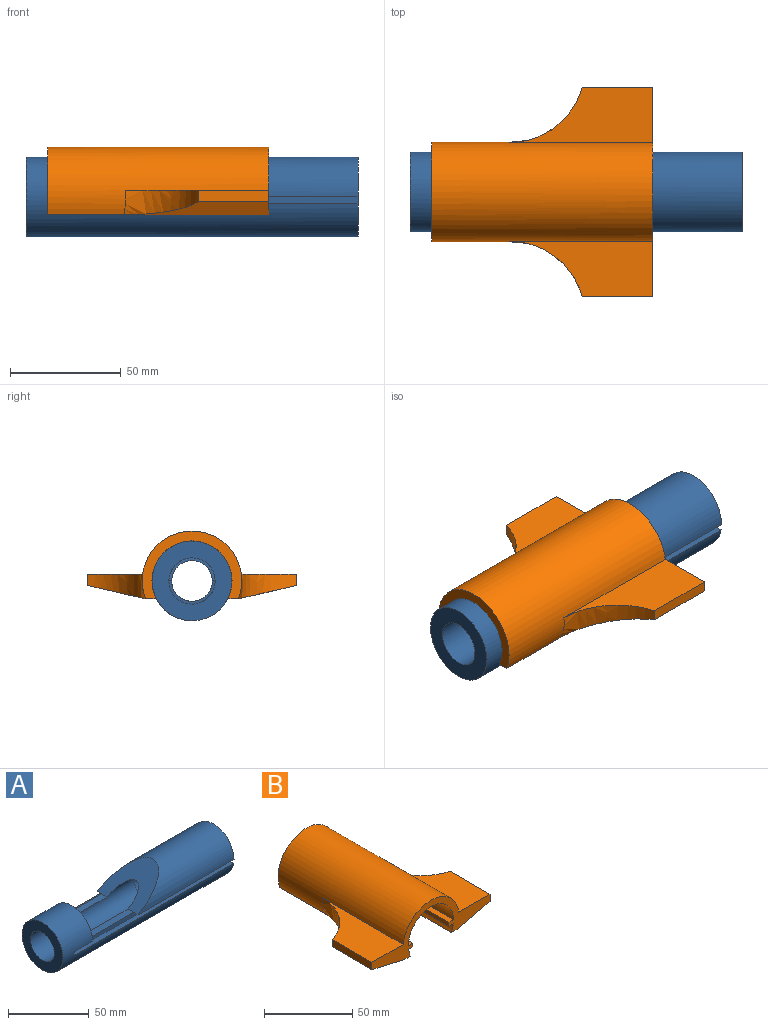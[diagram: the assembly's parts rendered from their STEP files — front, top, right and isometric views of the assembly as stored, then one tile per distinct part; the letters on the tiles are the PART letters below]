
ASSEMBLY  parts=2 mates=1
PART A: 23 faces, bbox 150x36x36 mm
  f0: cylinder r=9.2mm len=64.15mm, axis (-1,0,0), area 2259.1mm2, adj f1,f7,f8,f19,f22
  f1: plane 40x4.8mm, normal (0,0,1), area 192mm2, adj f0,f6,f8,f12,f19
  f2: cylinder r=18mm len=84.15mm, axis (-1,0,0), area 3636.5mm2, adj f3,f8,f9,f15
  f3: plane 36x36mm, normal (1,0,0), area 651.3mm2, adj f2,f4,f9,f11,f12,f15,f16,f17
  f4: cylinder r=18mm len=150mm, axis (-1,0,0), area 9099.9mm2, adj f3,f5,f6,f10,f11,f13,f14,f17
  f5: plane 36x36mm, normal (-1,0,0), area 674.8mm2, adj f4,f20
  f6: plane 36.01x18.01mm, normal (1,0,0), area 337.4mm2, adj f1,f4,f7,f10,f14,f20
  f7: plane 40x4.8mm, normal (0,0,1), area 192mm2, adj f0,f6,f8,f16,f19
  f8: plane 36x31.18mm, normal (-0.5,0,0.87), area 752mm2, adj f0,f1,f2,f7,f9,f15
  f9: plane 84.15x4mm, normal (0,0,-1), area 336.6mm2, adj f2,f3,f8,f12
  f10: plane 15.85x4mm, normal (0,0,-1), area 63.4mm2, adj f4,f6,f12,f13
  f11: plane 140x3.75mm, normal (0,0,1), area 524.8mm2, adj f3,f4,f12,f13
  f12: plane 140x3mm, normal (0,-1,0), area 420mm2, adj f1,f3,f9,f10,f11,f13
  f13: plane 4x3mm, normal (1,0,0), area 11.7mm2, adj f4,f10,f11,f12
  f14: plane 15.85x4mm, normal (0,0,-1), area 63.4mm2, adj f4,f6,f16,f18
  f15: plane 84.15x4mm, normal (0,0,-1), area 336.6mm2, adj f2,f3,f8,f16
  f16: plane 140x3mm, normal (0,1,0), area 420mm2, adj f3,f7,f14,f15,f17,f18
  f17: plane 140x3.75mm, normal (0,0,1), area 524.8mm2, adj f3,f4,f16,f18
  f18: plane 4x3mm, normal (1,0,0), area 11.7mm2, adj f4,f14,f16,f17
  f19: plane 20.91x10.53mm, normal (-1,0,0), area 38.6mm2, adj f0,f1,f7,f20
  f20: cylinder r=10.45mm len=25.85mm, axis (-1,0,0), area 1697.1mm2, adj f5,f6,f19
  f21: cylinder r=10.45mm len=60mm, axis (-1,0,0), area 3939.6mm2, adj f3,f22
  f22: plane 20.9x20.9mm, normal (1,0,0), area 77.2mm2, adj f0,f21
PART B: 22 faces, bbox 97x102.4x48.5 mm
  f0: cylinder r=22.5mm len=100mm, axis (0,1,0), area 7250.8mm2, adj f10,f11,f12,f13,f14,f17,f20,f21
  f1: cylinder r=18.1mm len=100mm, axis (0,1,0), area 565.9mm2, adj f2,f11,f12,f13
  f2: plane 100x3.5mm, normal (0,0,-1), area 349.7mm2, adj f1,f3,f12,f13
  f3: plane 100x2.7mm, normal (1,0,0), area 270mm2, adj f2,f4,f12,f13
  f4: plane 100x3.7mm, normal (0,0,1), area 370mm2, adj f3,f5,f12,f13
  f5: cylinder r=18.1mm len=100mm, axis (0,1,0), area 5686.3mm2, adj f4,f6,f12,f13
  f6: plane 100x3.7mm, normal (0,0,1), area 370mm2, adj f5,f7,f12,f13
  f7: plane 100x2.7mm, normal (-1,0,0), area 270mm2, adj f6,f8,f12,f13
  f8: plane 100x3.5mm, normal (0,0,-1), area 349.7mm2, adj f7,f9,f12,f13
  f9: cylinder r=18.1mm len=100mm, axis (0,1,0), area 565.9mm2, adj f8,f10,f12,f13
  f10: plane 100x4.8mm, normal (0,0,-1), area 480.2mm2, adj f0,f9,f12,f13,f15
  f11: plane 100x4.8mm, normal (0,0,-1), area 480.2mm2, adj f0,f1,f12,f13,f19
  f12: plane 94.6x30.57mm, normal (0,-1,0), area 771.4mm2, adj f0,f1,f2,f3,f4,f5,f6,f7
  f13: plane 45x30.57mm, normal (0,1,0), area 373.3mm2, adj f0,f1,f2,f3,f4,f5,f6,f7
  f14: plane 65.77x25.97mm, normal (0,0,1), area 1013.2mm2, adj f0,f12,f16,f20
  f15: plane 67.91x28.71mm, normal (0.23,0,-0.97), area 1106.6mm2, adj f10,f12,f16,f20
  f16: plane 31.91x5.01mm, normal (1,0,0), area 159.5mm2, adj f12,f14,f15,f20
  f17: plane 65.81x26.01mm, normal (0,0,1), area 1013.2mm2, adj f0,f12,f18,f21
  f18: plane 31.91x5.01mm, normal (-1,0,0), area 159.5mm2, adj f12,f17,f19,f21
  f19: plane 67.9x28.7mm, normal (-0.23,0,-0.97), area 1106.7mm2, adj f11,f12,f18,f21
  f20: bspline ~33.79x33.41mm, area 424.8mm2, adj f0,f14,f15,f16
  f21: bspline ~33.79x33.41mm, area 424.8mm2, adj f0,f17,f18,f19
PLACE A t=(-32.58,32.31,-6.68)mm fixed
PLACE B rot(axis=(0,0,1),90deg) t=(-22.85,32.31,-6.68)mm
MATE slider B.f0 <-> A.f2  axis (1,0,0) through (77.15,32.31,-6.68)mm
